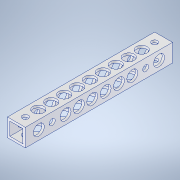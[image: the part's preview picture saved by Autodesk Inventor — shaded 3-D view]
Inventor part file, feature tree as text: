
AUTODESK INVENTOR PART (.ipt)
format: ipt  version: 2020.3 (Build 243373000, 373)  size: 223,744 bytes
history: native  units: mm
features: sketch x5, hole x4, other x1, extrude x1
ambient origin geometry x8: Origin, YZ Plane, XZ Plane, XY Plane, X Axis, Y Axis, Z Axis, Center Point
bodies: Body1 (feature_tree)
feature tree (11):
  other  "ソリッド1"
  extrude  "押し出し1"  Depth=9.0mm
  hole  "穴1"  [1 undecoded]
  hole  "穴2"  [1 undecoded]
  hole  "穴3"  [1 undecoded]
  hole  "穴4"  [1 undecoded]
  sketch  "スケッチ1"
  sketch  "スケッチ2"
  sketch  "スケッチ3"
  sketch  "スケッチ4"
  sketch  "スケッチ5"
note: 4 required parameter values undecoded (feature->parameter linkage not recoverable at this tier; creation-order binding heuristic only, values carry confidence <= 0.55)
